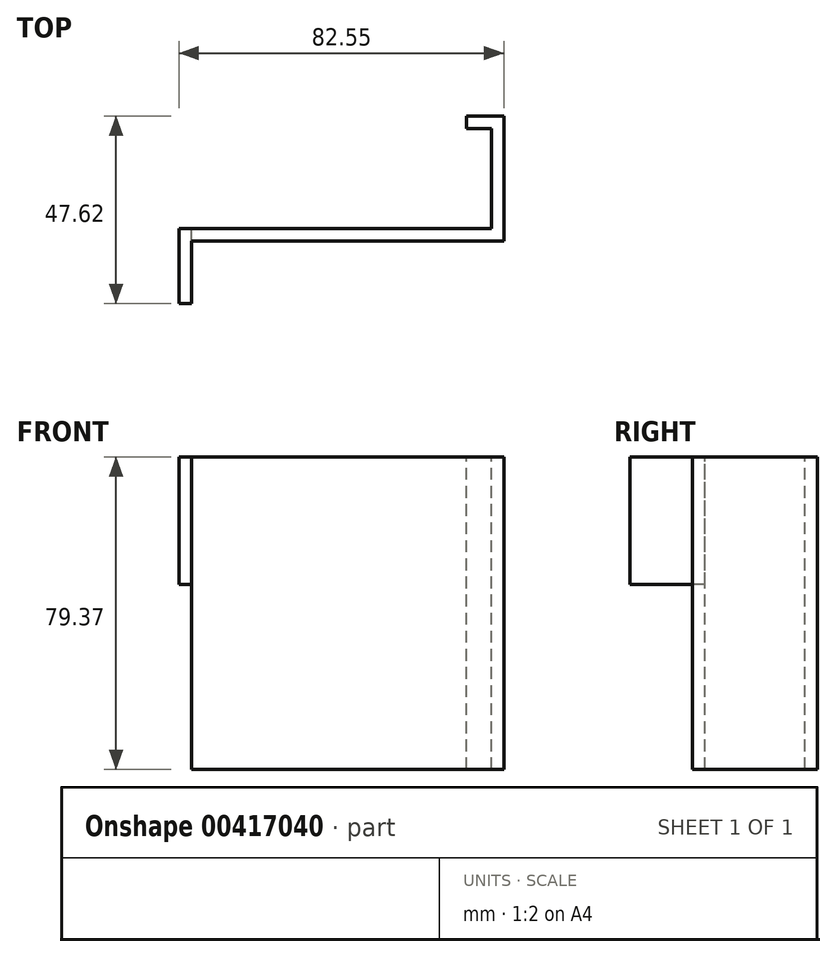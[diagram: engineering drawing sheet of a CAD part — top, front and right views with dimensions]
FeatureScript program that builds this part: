
annotation { "Feature Type Name" : "Feature", "Feature Type Description" : "" }
export const myFeature = defineFeature(function(context is Context, id is Id, definition is map)
    precondition{}
    {
        {
            var Q0;
            Q0=qCreatedBy(makeId("Front.planeOp"),FACE);
            var sketch = newSketch(context, id + "F0", { "sketchPlane" : qUnion([Q0])});
            skLineSegment(sketch, "E0.bottom", {"start": v(-28.68, 42.68) * mm, "end": v(53.87, 42.68) * mm});
            skLineSegment(sketch, "E0.top", {"start": v(-28.68, -33.52) * mm, "end": v(53.87, -33.52) * mm});
            skLineSegment(sketch, "E0.left", {"start": v(-28.68, 42.68) * mm, "end": v(-28.68, -33.52) * mm});
            skLineSegment(sketch, "E0.right", {"start": v(53.87, 42.68) * mm, "end": v(53.87, -33.52) * mm});
            skSolve(sketch);
        }
        {
            var Q0;
            Q0=makeQuery(id+"F0.imprint","IMPRINT",FACE,{"disambiguationData":[TD([[makeQuery(id+"F0.imprint","IMPRINT",EDGE,{"derivedFrom":sQuery(id+"F0.wireOp",EDGE,"E0.bottom")}),-1.0]])]});
            extrude(context, id + "F1", {"entities" : qUnion([Q0]), "depth" : 31.75 * mm});
        }
        {
            var Q0;
            Q0=makeQuery(id+"F1.opExtrude","SWEPT_FACE",FACE,{"disambiguationData":[OSD([sQuery(id+"F0.wireOp",EDGE,"E0.bottom")])]});
            var sketch = newSketch(context, id + "F2", { "sketchPlane" : qUnion([Q0])});
            skLineSegment(sketch, "E1", {"start": v(-0.78, -31.75) * mm, "end": v(-0.78, -28.57) * mm, "construction": true});
            skLineSegment(sketch, "E2", {"start": v(53.87, -15.88) * mm, "end": v(50.7, -15.88) * mm, "construction": true});
            skLineSegment(sketch, "E3", {"start": v(-28.68, -28.57) * mm, "end": v(53.87, -28.57) * mm});
            skLineSegment(sketch, "E4", {"start": v(50.7, -31.75) * mm, "end": v(50.7, 0) * mm});
            skSolve(sketch);
        }
        {
            var Q0;
            {var subQ1=sQuery(id+"F0.wireOp",EDGE,"E0.bottom");var subQ4=sQuery(id+"F2.wireOp",EDGE,"E4");var subQ6=makeQuery(id+"F1.opExtrude","CAP_EDGE",EDGE,{"disambiguationData":[OSD([subQ1])],"isStart":true});var subQ7=makeQuery(id+"F2.imprint","INTERSECT",VERTEX,{"derivedFrom":[subQ6,subQ4]});Q0=makeQuery(id+"F2.imprint","IMPRINT",FACE,{"disambiguationData":[TD([[makeQuery(id+"F2.imprint","IMPRINT",EDGE,{"disambiguationData":[TD([[subQ7,1.0]])],"derivedFrom":subQ4}),1.0]])]});}
            extrude(context, id + "F3", {"entities" : qUnion([Q0]), "operationType" : NewBodyOperationType.REMOVE, "oppositeDirection" : true, "depth" : 101.6 * mm});
        }
        {
            var Q0;
            Q0=makeQuery(id+"F1.opExtrude","CAP_FACE",FACE,{"disambiguationData":[OSD([sQuery(id+"F0.wireOp",EDGE,"E0.bottom"),sQuery(id+"F0.wireOp",EDGE,"E0.top"),sQuery(id+"F0.wireOp",EDGE,"E0.left"),sQuery(id+"F0.wireOp",EDGE,"E0.right")])],"isStart":true});
            var sketch = newSketch(context, id + "F4", { "sketchPlane" : qUnion([Q0])});
            skPoint(sketch, "E5.oppositeSnap0", {"position": v(-52.28, 42.68) * mm});
            skLineSegment(sketch, "E5.bottom", {"start": v(-53.87, -33.52) * mm, "end": v(-44.34, -33.52) * mm});
            skLineSegment(sketch, "E5.top", {"start": v(-53.87, 42.68) * mm, "end": v(-44.34, 42.68) * mm});
            skLineSegment(sketch, "E5.left", {"start": v(-53.87, -33.52) * mm, "end": v(-53.87, 42.68) * mm});
            skLineSegment(sketch, "E5.right", {"start": v(-44.34, -33.52) * mm, "end": v(-44.34, 42.68) * mm});
            skSolve(sketch);
        }
        {
            var Q0;
            {var subQ2=sQuery(id+"F4.wireOp",EDGE,"E5.right");Q0=makeQuery(id+"F4.imprint","IMPRINT",FACE,{"disambiguationData":[TD([[makeQuery(id+"F4.imprint","IMPRINT",EDGE,{"derivedFrom":subQ2}),1.0]])]});}
            extrude(context, id + "F5", {"entities" : qUnion([Q0]), "operationType" : NewBodyOperationType.ADD, "oppositeDirection" : true, "depth" : 3.17 * mm});
        }
        {
            var Q0;
            Q0=makeQuery(id+"F5.boolean.opBoolean","MERGE",FACE,{"derivedFrom":[makeQuery(id+"F1.opExtrude","SWEPT_FACE",FACE,{"disambiguationData":[OSD([sQuery(id+"F0.wireOp",EDGE,"E0.bottom")])]}),makeQuery(id+"F5.opExtrude","SWEPT_FACE",FACE,{"disambiguationData":[OSD([sQuery(id+"F4.wireOp",EDGE,"E5.top")])]})]});
            var sketch = newSketch(context, id + "F6", { "sketchPlane" : qUnion([Q0])});
            skLineSegment(sketch, "E6.bottom", {"start": v(53.87, -31.75) * mm, "end": v(-28.68, -31.75) * mm});
            skLineSegment(sketch, "E6.top", {"start": v(53.87, 0) * mm, "end": v(-28.68, 0) * mm});
            skLineSegment(sketch, "E6.left", {"start": v(53.87, -31.75) * mm, "end": v(53.87, 0) * mm});
            skLineSegment(sketch, "E6.right", {"start": v(-28.68, -31.75) * mm, "end": v(-28.68, 0) * mm});
            skSolve(sketch);
        }
        {
            var Q0;
            {var subQ3=makeQuery(id+"F3.boolean.opBoolean","COPY",EDGE,{"derivedFrom":makeQuery(id+"F3.opExtrude","CAP_EDGE",EDGE,{"disambiguationData":[OSD([sQuery(id+"F2.wireOp",EDGE,"E3")])],"isStart":true})});Q0=makeQuery(id+"F6.imprint","IMPRINT",FACE,{"disambiguationData":[TD([[makeQuery(id+"F6.imprint","IMPRINT",EDGE,{"derivedFrom":subQ3}),1.0]])]});}
            var Q1;
            {var subQ5=sQuery(id+"F6.wireOp",EDGE,"E6.bottom");Q1=makeQuery(id+"F6.imprint","IMPRINT",FACE,{"disambiguationData":[TD([[makeQuery(id+"F6.imprint","IMPRINT",EDGE,{"derivedFrom":subQ5}),1.0]])]});}
            extrude(context, id + "F7", {"entities" : qUnion([Q0, Q1]), "operationType" : NewBodyOperationType.ADD, "depth" : 3.17 * mm});
        }
        {
            var Q0;
            Q0=makeQuery(id+"F7.boolean.opBoolean","MERGE",FACE,{"derivedFrom":[makeQuery(id+"F1.opExtrude","SWEPT_FACE",FACE,{"disambiguationData":[OSD([sQuery(id+"F0.wireOp",EDGE,"E0.left")])]}),makeQuery(id+"F7.opExtrude","SWEPT_FACE",FACE,{"disambiguationData":[OSD([sQuery(id+"F6.wireOp",EDGE,"E6.right")])]})]});
            var sketch = newSketch(context, id + "F8", { "sketchPlane" : qUnion([Q0])});
            skLineSegment(sketch, "E7.bottom", {"start": v(28.57, -33.52) * mm, "end": v(47.62, -33.52) * mm});
            skLineSegment(sketch, "E7.top", {"start": v(28.57, 45.85) * mm, "end": v(47.62, 45.85) * mm});
            skLineSegment(sketch, "E7.left", {"start": v(28.57, -33.52) * mm, "end": v(28.57, 45.85) * mm});
            skLineSegment(sketch, "E7.right", {"start": v(47.62, -33.52) * mm, "end": v(47.62, 45.85) * mm});
            skSolve(sketch);
        }
        {
            var Q0;
            {var subQ2=sQuery(id+"F8.wireOp",EDGE,"E7.right");Q0=makeQuery(id+"F8.imprint","IMPRINT",FACE,{"disambiguationData":[TD([[makeQuery(id+"F8.imprint","IMPRINT",EDGE,{"derivedFrom":subQ2}),1.0]])]});}
            extrude(context, id + "F9", {"entities" : qUnion([Q0]), "operationType" : NewBodyOperationType.ADD, "oppositeDirection" : true, "depth" : 3.17 * mm});
        }
        {
            var Q0;
            {var subQ0=sQuery(id+"F6.wireOp",EDGE,"E6.right");var subQ1=sQuery(id+"F0.wireOp",EDGE,"E0.left");Q0=makeQuery(id+"F9.boolean.opBoolean","MERGE",FACE,{"derivedFrom":[makeQuery(id+"F7.boolean.opBoolean","MERGE",FACE,{"derivedFrom":[makeQuery(id+"F1.opExtrude","SWEPT_FACE",FACE,{"disambiguationData":[OSD([subQ1])]}),makeQuery(id+"F7.opExtrude","SWEPT_FACE",FACE,{"disambiguationData":[OSD([subQ0])]})]}),makeQuery(id+"F9.opExtrude","CAP_FACE",FACE,{"disambiguationData":[OSD([subQ1,sQuery(id+"F6.wireOp",EDGE,"E6.bottom"),subQ0,sQuery(id+"F8.wireOp",EDGE,"E7.bottom"),sQuery(id+"F8.wireOp",EDGE,"E7.top"),sQuery(id+"F8.wireOp",EDGE,"E7.right")])],"isStart":true})]});}
            var sketch = newSketch(context, id + "F10", { "sketchPlane" : qUnion([Q0])});
            skLineSegment(sketch, "E8.bottom", {"start": v(28.57, -33.52) * mm, "end": v(47.62, -33.52) * mm});
            skLineSegment(sketch, "E8.top", {"start": v(28.57, 13.47) * mm, "end": v(47.62, 13.47) * mm});
            skLineSegment(sketch, "E8.left", {"start": v(28.57, -33.52) * mm, "end": v(28.57, 13.47) * mm});
            skLineSegment(sketch, "E8.right", {"start": v(47.62, -33.52) * mm, "end": v(47.62, 13.47) * mm});
            skSolve(sketch);
        }
        {
            var Q0;
            Q0=makeQuery(id+"F10.imprint","IMPRINT",FACE,{"disambiguationData":[TD([[makeQuery(id+"F10.imprint","IMPRINT",EDGE,{"derivedFrom":sQuery(id+"F10.wireOp",EDGE,"E8.bottom")}),-1.0]])]});
            extrude(context, id + "F11", {"entities" : qUnion([Q0]), "operationType" : NewBodyOperationType.REMOVE, "oppositeDirection" : true, "depth" : 3.17 * mm});
        }
    });
